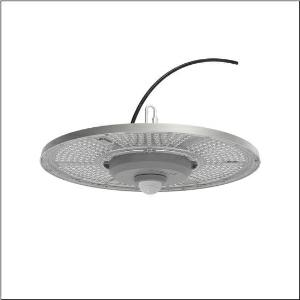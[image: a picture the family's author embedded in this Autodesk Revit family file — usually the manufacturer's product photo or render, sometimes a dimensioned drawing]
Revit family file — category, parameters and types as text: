
# Revit family: highbay_31-l_51hc427a4mmb01
name_source: partatom
category: Lighting Fixtures
units: mm (PartAtom-declared; Revit-internal decimal feet)

## family parameters
Cut with Voids When Loaded = No
Host = Face
Light Source = No
Part Type = Normal
Room Calculation Point = No
Round Connector Dimension = Use Diameter
Shared = No

## types (1)
- Highbay 31-L (1 x LED, 28000 lm, 187 W, 4000K)
    Apparent Load = 187 VA
    CIE Flux Codes = 83 98 100 100 100
    Color Rendering = 80
    Color Temperature = 4000K
    Default Elevation = 1800 mm
    Description = Highbay 31-L, high bay luminaire, primary light control with lens, of PC, primary optical cover: cover panel, of PC, transparent, light emission: direct distribution, primary light characteristic: rotationally symmetric, installation type: suspended mounting, surface-mounted, LED, rated luminous flux: 28.000lm, luminous efficacy: 150lm/W, light colour: 840, colour temperature: 4000K, control gear: ON/OFF, with cable, 3x 1.0mm², free wire ends, mains connection: 220..240V, AC, 50/60Hz, cable length: 1,5m, rated input power: 187W, housing, rotationally symmetric, of diecast aluminium, powder-coated, grey aluminium (RAL 9007), with hook on luminaire side, incl. screw, diameter: 406mm, PIR sensor, protection rating (complete): IP65, insulation class (complete): insulation class I (protective earthing), certification: CE, ENEC, UKCA, protection symbol: D, impact resistance: IK08, permissible operating ambient temperature: -30..+45°C, corresponds to IFS (International Featured Standards) requirements for safety and quality in the food industry, packaging unit: 1 piece
    Height = 160 mm
    Lamp = 1 x LED
    Lamp Light Flux = 28000 lm
    Lamp Power = 187 W
    Lamp count = 1
    Length = 406 mm
    Luminous efficacy = 150 lm/W
    Manufacturer = Siteco
    ModVariant = No
    Model = 51HC427A4MMB01
    Mounting Place = Ceiling
    Mounting Type = Pendant
    Number of Poles = 1
    OnlyDefault = Yes
    Power Factor = 1
    Product Name = Highbay 31-L
    Product group = high bay luminaire
    ProductGroupID = 902
    Protection Class = Protection class I
    Protection Degree = IP 65
    RLX_Detail_Level = 1
    RLX_Emergency_Light_Flux = 0 lm
    RLX_Emergency_Type = 0
    RLX_Emergency_Type_DB = No
    RlxData = <blob elided: 124993 chars, md5=ee857094>
    Socket = socket
    Standby Power = 0 W
    System Light Flux = 28000 lm
    System Power = 187 W
    Type Comments = Product without accessories
    Type Image = l_1410009.jpg
    URL = http://relux.com
    VarID = ---
    Voltage = 0 V
    Weight = 0.00 kg
    Width = 0 mm  [stored 0 ft]

note: [stored X ft] marks values corroborated as IEEE doubles in the binary element streams (Revit-internal decimal feet)

## geometry (parser evidence)
native form markers: Blend x4, Sweep x10
no freeform markers — native parametric forms only
